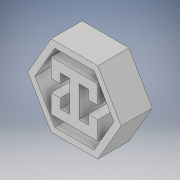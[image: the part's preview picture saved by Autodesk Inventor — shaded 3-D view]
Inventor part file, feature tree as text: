
AUTODESK INVENTOR PART (.ipt)
format: ipt  version: 2019 (Build 230136000, 136)  size: 140,800 bytes
history: native  units: mm
features: extrude x1
ambient origin geometry x8: Origin, YZ Plane, XZ Plane, XY Plane, X Axis, Y Axis, Z Axis, Center Point
bodies: Solid1 (feature_tree)
feature tree (1):
  extrude  "Extrusion1"  Depth=15.0mm
